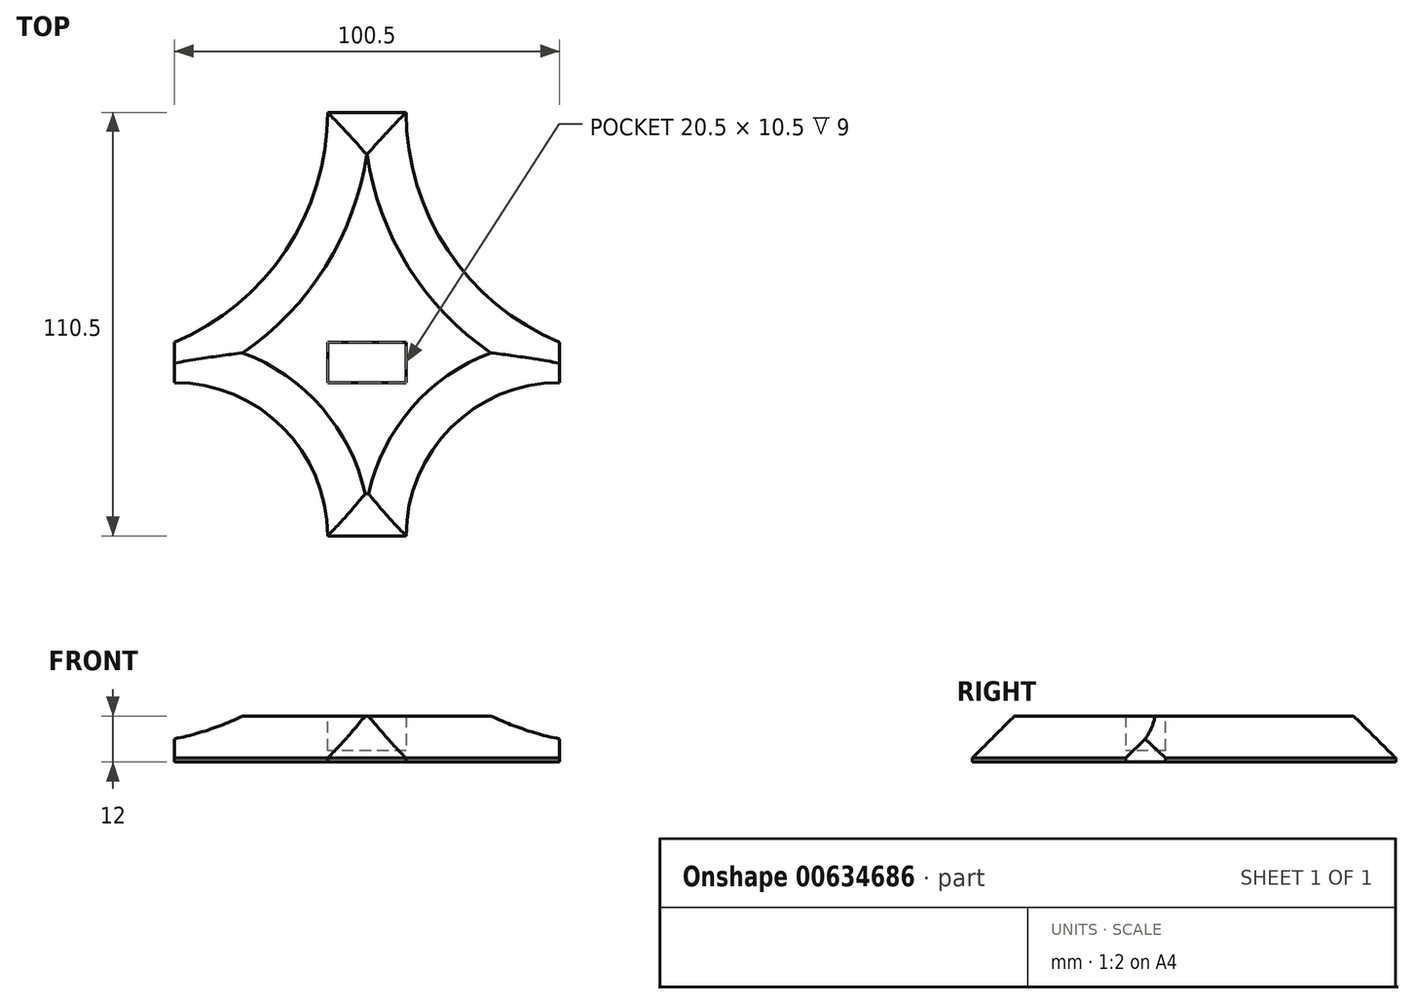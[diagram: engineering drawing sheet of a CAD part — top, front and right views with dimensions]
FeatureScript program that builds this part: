
annotation { "Feature Type Name" : "Feature", "Feature Type Description" : "" }
export const myFeature = defineFeature(function(context is Context, id is Id, definition is map)
    precondition{}
    {
        {
            var Q0;
            Q0=qCreatedBy(makeId("Top.planeOp"),FACE);
            var sketch = newSketch(context, id + "F0", { "sketchPlane" : qUnion([Q0])});
            skLineSegment(sketch, "E0", {"start": v(0, 0) * mm, "end": v(0, 10.5) * mm});
            skLineSegment(sketch, "E1", {"start": v(0, 10.5) * mm, "end": v(20.5, 10.5) * mm});
            skLineSegment(sketch, "E2", {"start": v(20.5, 10.5) * mm, "end": v(20.5, 0) * mm});
            skLineSegment(sketch, "E3", {"start": v(0, 0) * mm, "end": v(20.5, 0) * mm});
            skLineSegment(sketch, "E4.top", {"start": v(0, 70.5) * mm, "end": v(20.5, 70.5) * mm});
            skLineSegment(sketch, "E4.left", {"start": v(0, 10.5) * mm, "end": v(0, 70.5) * mm});
            skLineSegment(sketch, "E4.right", {"start": v(20.5, 10.5) * mm, "end": v(20.5, 70.5) * mm});
            skLineSegment(sketch, "E5.bottom", {"start": v(20.5, 10.5) * mm, "end": v(60.5, 10.5) * mm});
            skLineSegment(sketch, "E5.top", {"start": v(20.5, 0) * mm, "end": v(60.5, 0) * mm});
            skLineSegment(sketch, "E5.right", {"start": v(60.5, 10.5) * mm, "end": v(60.5, 0) * mm});
            skLineSegment(sketch, "E6.top", {"start": v(0, -40) * mm, "end": v(20.5, -40) * mm});
            skLineSegment(sketch, "E6.left", {"start": v(0, 0) * mm, "end": v(0, -40) * mm});
            skLineSegment(sketch, "E6.right", {"start": v(20.5, 0) * mm, "end": v(20.5, -40) * mm});
            skLineSegment(sketch, "E7.bottom", {"start": v(0, 0) * mm, "end": v(-40, 0) * mm});
            skLineSegment(sketch, "E7.top", {"start": v(0, 10.5) * mm, "end": v(-40, 10.5) * mm});
            skLineSegment(sketch, "E7.right", {"start": v(-40, 0) * mm, "end": v(-40, 10.5) * mm});
            skArc(sketch, "E8", {"start": v(20.5, 70.5) * mm, "mid": v(31.42, 34.44) * mm, "end": v(60.5, 10.5) * mm});
            skArc(sketch, "E9", {"start": v(-40, 10.5) * mm, "mid": v(-10.92, 34.44) * mm, "end": v(0, 70.5) * mm});
            skArc(sketch, "E10", {"start": v(0, -40) * mm, "mid": v(-11.72, -11.72) * mm, "end": v(-40, 0) * mm});
            skArc(sketch, "E11", {"start": v(60.5, 0) * mm, "mid": v(32.22, -11.72) * mm, "end": v(20.5, -40) * mm});
            skLineSegment(sketch, "E12", {"start": v(20.5, 0) * mm, "end": v(0, 10.5) * mm});
            skSolve(sketch);
        }
        {
            var Q0;
            Q0 = qSketchRegion(id + "F0", true);
            extrude(context, id + "F1", {"entities" : qUnion([Q0]), "depth" : 12 * mm, "offsetDistance" : 25 * mm});
        }
        {
            var Q0;
            Q0=qCreatedBy(makeId("Top.planeOp"),FACE);
            var sketch = newSketch(context, id + "F2", { "sketchPlane" : qUnion([Q0])});
            skLineSegment(sketch, "E13", {"start": v(0, 0) * mm, "end": v(20.5, 0) * mm});
            skLineSegment(sketch, "E14", {"start": v(20.5, 0) * mm, "end": v(20.5, 10.5) * mm});
            skLineSegment(sketch, "E15", {"start": v(20.5, 10.5) * mm, "end": v(0, 10.5) * mm});
            skLineSegment(sketch, "E16", {"start": v(0, 10.5) * mm, "end": v(0, 0) * mm});
            skSolve(sketch);
        }
        {
            var Q0;
            Q0 = qSketchRegion(id + "F2", true);
            extrude(context, id + "F3", {"entities" : qUnion([Q0]), "operationType" : NewBodyOperationType.ADD, "depth" : 3 * mm, "offsetDistance" : 25 * mm});
        }
        {
            var Q0;
            Q0=makeQuery(id+"F1.opExtrude","CAP_EDGE",EDGE,{"disambiguationData":[OSD([sQuery(id+"F0.wireOp",EDGE,"E6.top")])],"isStart":false});
            var Q1;
            Q1=makeQuery(id+"F1.opExtrude","CAP_EDGE",EDGE,{"disambiguationData":[OSD([sQuery(id+"F0.wireOp",EDGE,"E11")])],"isStart":false});
            var Q2;
            Q2=makeQuery(id+"F1.opExtrude","CAP_EDGE",EDGE,{"disambiguationData":[OSD([sQuery(id+"F0.wireOp",EDGE,"E10")])],"isStart":false});
            var Q3;
            Q3=makeQuery(id+"F1.opExtrude","CAP_EDGE",EDGE,{"disambiguationData":[OSD([sQuery(id+"F0.wireOp",EDGE,"E7.right")])],"isStart":false});
            var Q4;
            Q4=makeQuery(id+"F1.opExtrude","CAP_EDGE",EDGE,{"disambiguationData":[OSD([sQuery(id+"F0.wireOp",EDGE,"E9")])],"isStart":false});
            var Q5;
            Q5=makeQuery(id+"F1.opExtrude","CAP_EDGE",EDGE,{"disambiguationData":[OSD([sQuery(id+"F0.wireOp",EDGE,"E4.top")])],"isStart":false});
            var Q6;
            Q6=makeQuery(id+"F1.opExtrude","CAP_EDGE",EDGE,{"disambiguationData":[OSD([sQuery(id+"F0.wireOp",EDGE,"E8")])],"isStart":false});
            chamfer(context, id + "F4", {"entities" : qUnion([Q0, Q1, Q2, Q3, Q4, Q5, Q6]), "width" : 11 * mm});
        }
    });
